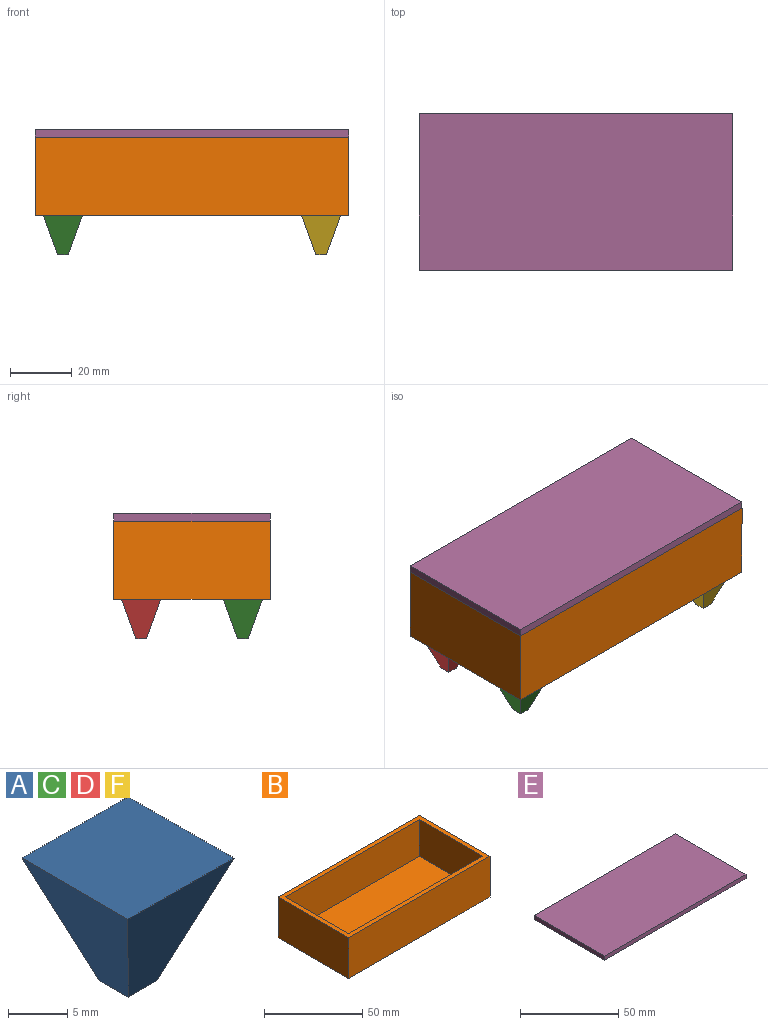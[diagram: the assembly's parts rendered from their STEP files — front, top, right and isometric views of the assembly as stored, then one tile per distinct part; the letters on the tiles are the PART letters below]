
ASSEMBLY  parts=6 mates=3
PART A: 6 faces, bbox 12.7x12.7x12.7 mm
  f0: plane 12.7x12.7mm, normal (0,0.94,-0.34), area 109.2mm2, adj f1,f3,f4,f5
  f1: plane 12.7x12.7mm, normal (-0.94,0,-0.34), area 109.2mm2, adj f0,f2,f4,f5
  f2: plane 12.7x12.7mm, normal (0,-0.94,-0.34), area 109.2mm2, adj f1,f3,f4,f5
  f3: plane 12.7x12.7mm, normal (0.94,0,-0.34), area 109.2mm2, adj f0,f2,f4,f5
  f4: plane 3.46x3.46mm, normal (0,0,-1), area 11.9mm2, adj f0,f1,f2,f3
  f5: plane 12.7x12.7mm, normal (0,0,1), area 161.3mm2, adj f0,f1,f2,f3
PART B: 11 faces, bbox 101.6x50.8x25.4 mm
  f0: plane 101.6x50.8mm, normal (0,0,1), area 748.4mm2, adj f1,f2,f3,f4,f6,f7,f8,f9
  f1: plane 101.6x25.4mm, normal (0,1,0), area 2580.6mm2, adj f0,f2,f4,f5
  f2: plane 50.8x25.4mm, normal (-1,0,0), area 1290.3mm2, adj f0,f1,f3,f5
  f3: plane 101.6x25.4mm, normal (0,-1,0), area 2580.6mm2, adj f0,f2,f4,f5
  f4: plane 50.8x25.4mm, normal (1,0,0), area 1290.3mm2, adj f0,f1,f3,f5
  f5: plane 101.6x50.8mm, normal (0,0,-1), area 5161.3mm2, adj f1,f2,f3,f4
  f6: plane 96.52x22.86mm, normal (0,-1,0), area 2206.4mm2, adj f0,f7,f9,f10
  f7: plane 45.72x22.86mm, normal (1,0,0), area 1045.2mm2, adj f0,f6,f8,f10
  f8: plane 96.52x22.86mm, normal (0,1,0), area 2206.4mm2, adj f0,f7,f9,f10
  f9: plane 45.72x22.86mm, normal (-1,0,0), area 1045.2mm2, adj f0,f6,f8,f10
  f10: plane 96.52x45.72mm, normal (0,0,1), area 4412.9mm2, adj f6,f7,f8,f9
PART C: same geometry as A
PART D: same geometry as A
PART E: 11 faces, bbox 101.6x50.8x5.1 mm
  f0: plane 101.6x50.8mm, normal (0,0,-1), area 748.4mm2, adj f1,f2,f3,f4,f6,f7,f8,f9
  f1: plane 101.6x2.54mm, normal (0,1,0), area 258.1mm2, adj f0,f2,f4,f5
  f2: plane 50.8x2.54mm, normal (-1,0,0), area 129mm2, adj f0,f1,f3,f5
  f3: plane 101.6x2.54mm, normal (0,-1,0), area 258.1mm2, adj f0,f2,f4,f5
  f4: plane 50.8x2.54mm, normal (1,0,0), area 129mm2, adj f0,f1,f3,f5
  f5: plane 101.6x50.8mm, normal (0,0,1), area 5161.3mm2, adj f1,f2,f3,f4
  f6: plane 96.52x2.54mm, normal (0,1,0), area 245.2mm2, adj f0,f7,f9,f10
  f7: plane 45.72x2.54mm, normal (1,0,0), area 116.1mm2, adj f0,f6,f8,f10
  f8: plane 96.52x2.54mm, normal (0,-1,0), area 245.2mm2, adj f0,f7,f9,f10
  f9: plane 45.72x2.54mm, normal (-1,0,0), area 116.1mm2, adj f0,f6,f8,f10
  f10: plane 96.52x45.72mm, normal (0,0,-1), area 4412.9mm2, adj f6,f7,f8,f9
PART F: same geometry as A
PLACE A rot(axis=(0,1,0),0deg) t=(29.23,35.96,-27.58)mm
PLACE B rot(axis=(0,1,0),0deg) t=(-8.79,-5.95,-27.58)mm
PLACE C rot(axis=(0,1,0),0deg) t=(-54.59,2.94,-27.58)mm
PLACE D rot(axis=(0,1,0),0deg) t=(-54.59,35.96,-27.58)mm
PLACE E rot(axis=(0,1,0),0deg) t=(-12.68,19.45,-2.18)mm
PLACE F rot(axis=(0,1,0),0deg) t=(29.23,2.94,-27.58)mm
MATE fastened C.f5 <-> B.f5  axis (0,0,1) through (-54.59,2.94,-27.58)mm
MATE planar C.f5 <-> B.f5  axis (0,0,1) through (-54.59,2.94,-27.58)mm
MATE fastened E.f3 <-> B.f3  axis (0,-1,0) through (-12.68,-5.95,-2.18)mm
